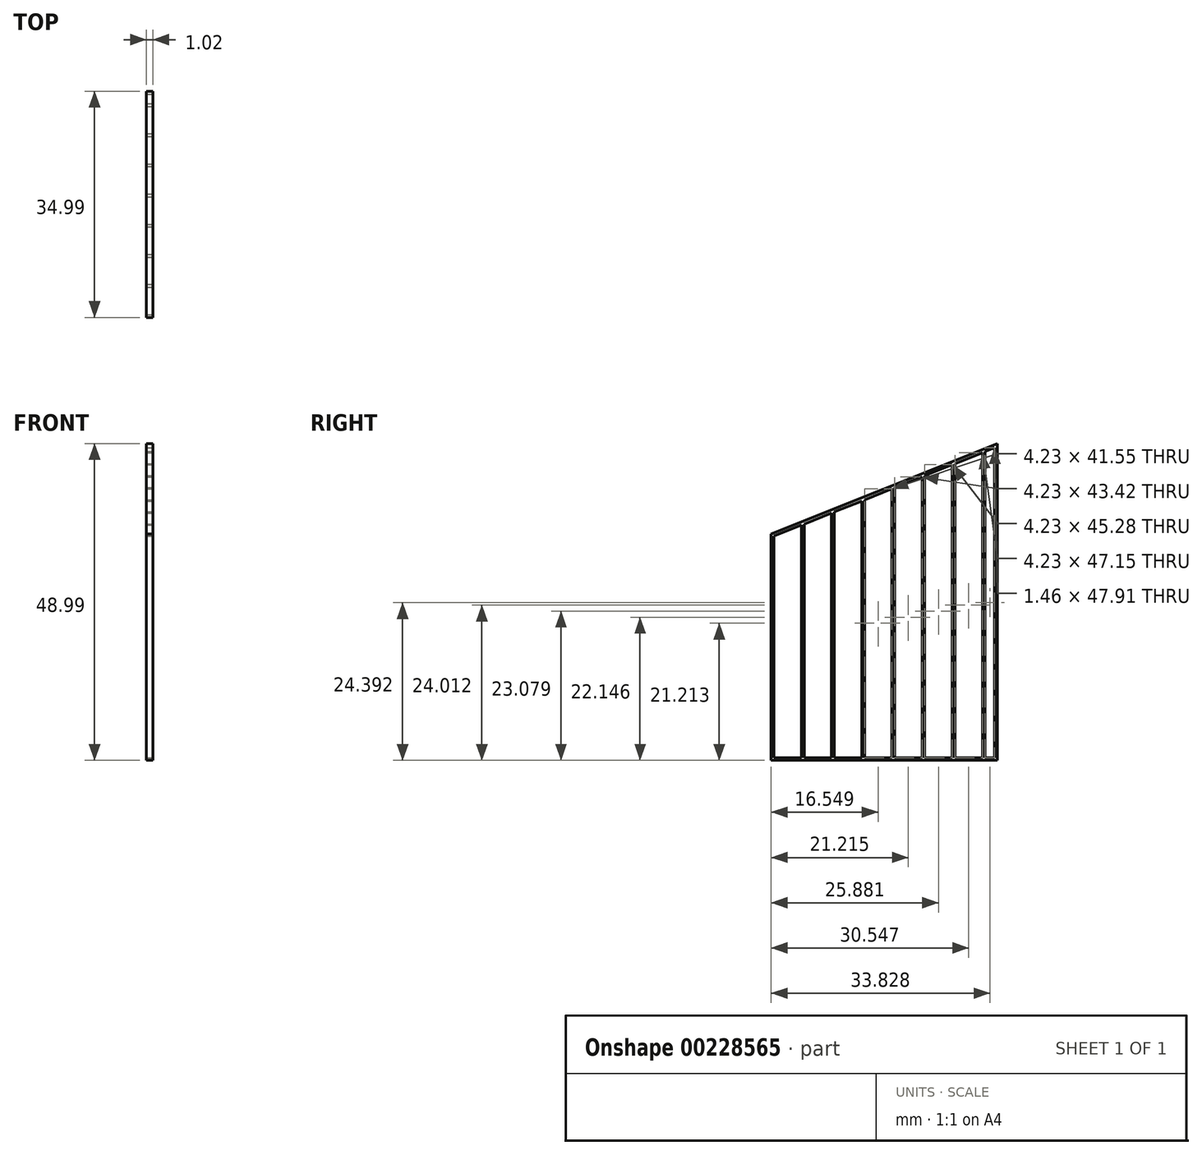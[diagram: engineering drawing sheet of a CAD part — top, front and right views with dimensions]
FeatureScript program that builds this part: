
annotation { "Feature Type Name" : "Feature", "Feature Type Description" : "" }
export const myFeature = defineFeature(function(context is Context, id is Id, definition is map)
    precondition{}
    {
        {
            var Q0;
            Q0=qCreatedBy(makeId("Right.planeOp"),FACE);
            var sketch = newSketch(context, id + "F0", { "sketchPlane" : qUnion([Q0])});
            skLineSegment(sketch, "E0", {"start": v(0, 0) * mm, "end": v(3048, 0) * mm});
            skLineSegment(sketch, "E1", {"start": v(3048, 0) * mm, "end": v(3048, 4267.2) * mm});
            skLineSegment(sketch, "E2", {"start": v(3048, 4267.2) * mm, "end": v(0, 3048) * mm});
            skLineSegment(sketch, "E3", {"start": v(0, 3048) * mm, "end": v(0, 0) * mm});
            skSolve(sketch);
        }
        {
            var Q0;
            Q0=makeQuery(id+"F0.imprint","IMPRINT",FACE,{"disambiguationData":[TD([[makeQuery(id+"F0.imprint","IMPRINT",EDGE,{"derivedFrom":sQuery(id+"F0.wireOp",EDGE,"E0")}),1.0]])]});
            extrude(context, id + "F1", {"entities" : qUnion([Q0]), "depth" : 88.9 * mm});
        }
        {
            var Q0;
            Q0=makeQuery(id+"F1.opExtrude","CAP_FACE",FACE,{"disambiguationData":[OSD([sQuery(id+"F0.wireOp",EDGE,"E0"),sQuery(id+"F0.wireOp",EDGE,"E1"),sQuery(id+"F0.wireOp",EDGE,"E2"),sQuery(id+"F0.wireOp",EDGE,"E3")])],"isStart":false});
            var sketch = newSketch(context, id + "F2", { "sketchPlane" : qUnion([Q0])});
            skLineSegment(sketch, "E4", {"start": v(38.1, 3022.2) * mm, "end": v(38.1, 38.1) * mm});
            skLineSegment(sketch, "E5", {"start": v(38.1, 38.1) * mm, "end": v(406.4, 38.1) * mm});
            skLineSegment(sketch, "E6", {"start": v(406.4, 38.1) * mm, "end": v(406.4, 3169.53) * mm});
            skLineSegment(sketch, "E7", {"start": v(406.4, 3169.53) * mm, "end": v(38.1, 3022.2) * mm});
            skLineSegment(sketch, "E8", {"start": v(444.5, 3184.77) * mm, "end": v(444.5, 38.1) * mm});
            skLineSegment(sketch, "E9", {"start": v(444.5, 38.1) * mm, "end": v(812.8, 38.1) * mm});
            skLineSegment(sketch, "E10", {"start": v(812.8, 38.1) * mm, "end": v(812.8, 3332.09) * mm});
            skLineSegment(sketch, "E11", {"start": v(812.8, 3332.09) * mm, "end": v(444.5, 3184.77) * mm});
            skLineSegment(sketch, "E12", {"start": v(850.9, 3347.33) * mm, "end": v(850.9, 38.1) * mm});
            skLineSegment(sketch, "E13", {"start": v(850.9, 38.1) * mm, "end": v(1219.2, 38.1) * mm});
            skLineSegment(sketch, "E14", {"start": v(1219.2, 38.1) * mm, "end": v(1219.2, 3494.65) * mm});
            skLineSegment(sketch, "E15", {"start": v(1219.2, 3494.65) * mm, "end": v(850.9, 3347.33) * mm});
            skLineSegment(sketch, "E16", {"start": v(1257.3, 3509.89) * mm, "end": v(1257.3, 38.1) * mm});
            skLineSegment(sketch, "E17", {"start": v(1257.3, 38.1) * mm, "end": v(1625.6, 38.1) * mm});
            skLineSegment(sketch, "E18", {"start": v(1625.6, 38.1) * mm, "end": v(1625.6, 3657.2) * mm});
            skLineSegment(sketch, "E19", {"start": v(1625.6, 3657.2) * mm, "end": v(1257.3, 3509.89) * mm});
            skLineSegment(sketch, "E20", {"start": v(1663.7, 3672.45) * mm, "end": v(1663.7, 38.1) * mm});
            skLineSegment(sketch, "E21", {"start": v(1663.7, 38.1) * mm, "end": v(2032, 38.1) * mm});
            skLineSegment(sketch, "E22", {"start": v(2032, 38.1) * mm, "end": v(2032, 3819.77) * mm});
            skLineSegment(sketch, "E23", {"start": v(2032, 3819.77) * mm, "end": v(1663.7, 3672.45) * mm});
            skLineSegment(sketch, "E24", {"start": v(2070.1, 3835) * mm, "end": v(2070.1, 38.1) * mm});
            skLineSegment(sketch, "E25", {"start": v(2070.1, 38.1) * mm, "end": v(2438.4, 38.1) * mm});
            skLineSegment(sketch, "E26", {"start": v(2438.4, 38.1) * mm, "end": v(2438.4, 3982.33) * mm});
            skLineSegment(sketch, "E27", {"start": v(2438.4, 3982.33) * mm, "end": v(2070.1, 3835) * mm});
            skLineSegment(sketch, "E28", {"start": v(2476.5, 3997.57) * mm, "end": v(2476.5, 38.1) * mm});
            skLineSegment(sketch, "E29", {"start": v(2476.5, 38.1) * mm, "end": v(2844.8, 38.1) * mm});
            skLineSegment(sketch, "E30", {"start": v(2844.8, 38.1) * mm, "end": v(2844.8, 4144.89) * mm});
            skLineSegment(sketch, "E31", {"start": v(2844.8, 4144.89) * mm, "end": v(2476.5, 3997.57) * mm});
            skLineSegment(sketch, "E32", {"start": v(2882.9, 4160.13) * mm, "end": v(2882.9, 38.1) * mm});
            skLineSegment(sketch, "E33", {"start": v(2882.9, 38.1) * mm, "end": v(3009.9, 38.1) * mm});
            skLineSegment(sketch, "E34", {"start": v(3009.9, 38.1) * mm, "end": v(3009.9, 4210.93) * mm});
            skLineSegment(sketch, "E35", {"start": v(3009.9, 4210.93) * mm, "end": v(2882.9, 4160.13) * mm});
            skSolve(sketch);
        }
        {
            var Q0;
            Q0=makeQuery(id+"F2.imprint","IMPRINT",FACE,{"disambiguationData":[TD([[makeQuery(id+"F2.imprint","IMPRINT",EDGE,{"derivedFrom":sQuery(id+"F2.wireOp",EDGE,"E4")}),1.0]])]});
            var Q1;
            Q1=makeQuery(id+"F2.imprint","IMPRINT",FACE,{"disambiguationData":[TD([[makeQuery(id+"F2.imprint","IMPRINT",EDGE,{"derivedFrom":sQuery(id+"F2.wireOp",EDGE,"E8")}),1.0]])]});
            var Q2;
            Q2=makeQuery(id+"F2.imprint","IMPRINT",FACE,{"disambiguationData":[TD([[makeQuery(id+"F2.imprint","IMPRINT",EDGE,{"derivedFrom":sQuery(id+"F2.wireOp",EDGE,"E12")}),1.0]])]});
            var Q3;
            Q3=makeQuery(id+"F2.imprint","IMPRINT",FACE,{"disambiguationData":[TD([[makeQuery(id+"F2.imprint","IMPRINT",EDGE,{"derivedFrom":sQuery(id+"F2.wireOp",EDGE,"E16")}),1.0]])]});
            var Q4;
            Q4=makeQuery(id+"F2.imprint","IMPRINT",FACE,{"disambiguationData":[TD([[makeQuery(id+"F2.imprint","IMPRINT",EDGE,{"derivedFrom":sQuery(id+"F2.wireOp",EDGE,"E20")}),1.0]])]});
            var Q5;
            Q5=makeQuery(id+"F2.imprint","IMPRINT",FACE,{"disambiguationData":[TD([[makeQuery(id+"F2.imprint","IMPRINT",EDGE,{"derivedFrom":sQuery(id+"F2.wireOp",EDGE,"E24")}),1.0]])]});
            var Q6;
            Q6=makeQuery(id+"F2.imprint","IMPRINT",FACE,{"disambiguationData":[TD([[makeQuery(id+"F2.imprint","IMPRINT",EDGE,{"derivedFrom":sQuery(id+"F2.wireOp",EDGE,"E28")}),1.0]])]});
            var Q7;
            Q7=makeQuery(id+"F2.imprint","IMPRINT",FACE,{"disambiguationData":[TD([[makeQuery(id+"F2.imprint","IMPRINT",EDGE,{"derivedFrom":sQuery(id+"F2.wireOp",EDGE,"E32")}),1.0]])]});
            extrude(context, id + "F3", {"entities" : qUnion([Q0, Q1, Q2, Q3, Q4, Q5, Q6, Q7]), "operationType" : NewBodyOperationType.REMOVE, "endBound" : BoundingType.THROUGH_ALL, "oppositeDirection" : true, "depth" : 25.4 * mm});
        }
        {
            var Q0;
            Q0=makeQuery(id+"F1.opExtrude","SWEPT_BODY",BODY,{"disambiguationData":[OSD([sQuery(id+"F0.wireOp",EDGE,"E0"),sQuery(id+"F0.wireOp",EDGE,"E1"),sQuery(id+"F0.wireOp",EDGE,"E2"),sQuery(id+"F0.wireOp",EDGE,"E3")])]});
            var Q1;
            Q1=qCreatedBy(makeId("Origin.pointOp"),VERTEX);
            transform(context, id + "F4", {"entities" : qUnion([Q0]), "transformType" : TransformType.SCALE_UNIFORMLY, "scale" : 1 / 87.1, "scalePoint" : qUnion([Q1]), "makeCopy" : false});
        }
    });
